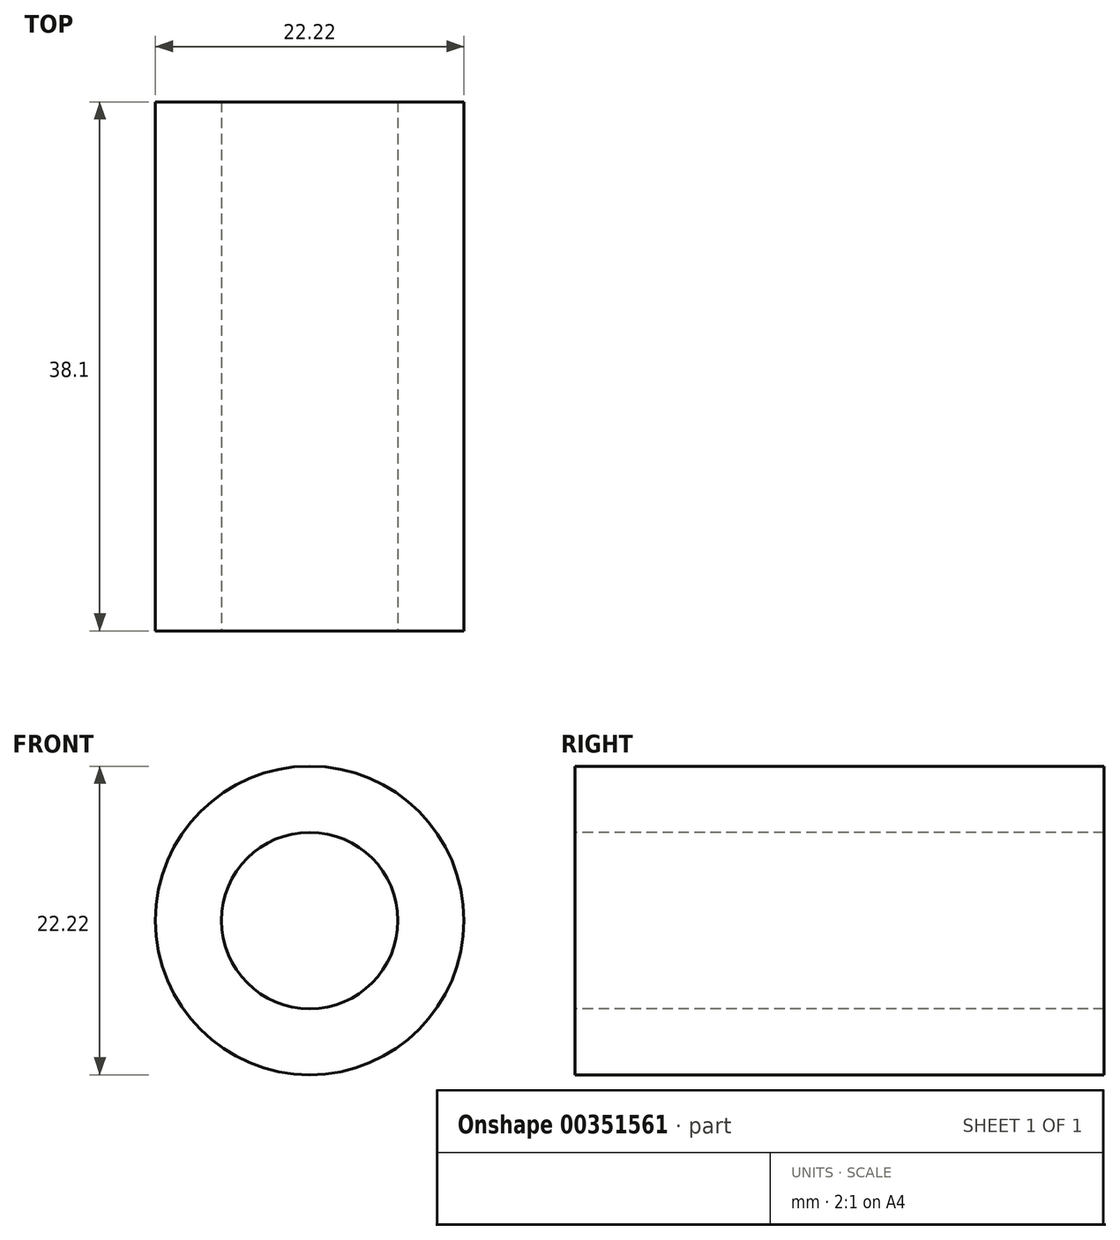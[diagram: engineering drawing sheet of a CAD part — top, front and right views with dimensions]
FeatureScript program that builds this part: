
annotation { "Feature Type Name" : "Feature", "Feature Type Description" : "" }
export const myFeature = defineFeature(function(context is Context, id is Id, definition is map)
    precondition{}
    {
        {
            var Q0;
            Q0=qCreatedBy(makeId("Front.planeOp"),FACE);
            var sketch = newSketch(context, id + "F0", { "sketchPlane" : qUnion([Q0])});
            skCircle(sketch, "E0", {"center": v(0, 0) * mm, "radius": 11.11 * mm});
            skSolve(sketch);
        }
        {
            var Q0;
            Q0 = qSketchRegion(id + "F0", true);
            extrude(context, id + "F1", {"entities" : qUnion([Q0]), "depth" : 38.1 * mm, "symmetric" : true});
        }
        {
            var Q0;
            Q0=makeQuery(id+"F1.opExtrude","CAP_FACE",FACE,{"disambiguationData":[OSD([sQuery(id+"F0.wireOp",EDGE,"E0")])],"isStart":false});
            var sketch = newSketch(context, id + "F2", { "sketchPlane" : qUnion([Q0])});
            skCircle(sketch, "E1", {"center": v(0, 0) * mm, "radius": 6.35 * mm});
            skSolve(sketch);
        }
        {
            var Q0;
            Q0=makeQuery(id+"F2.imprint","IMPRINT",FACE,{"disambiguationData":[TD([[makeQuery(id+"F2.imprint","IMPRINT",EDGE,{"derivedFrom":sQuery(id+"F2.wireOp",EDGE,"E1")}),1.0]])]});
            extrude(context, id + "F3", {"entities" : qUnion([Q0]), "operationType" : NewBodyOperationType.REMOVE, "oppositeDirection" : true, "depth" : 38.1 * mm});
        }
    });
